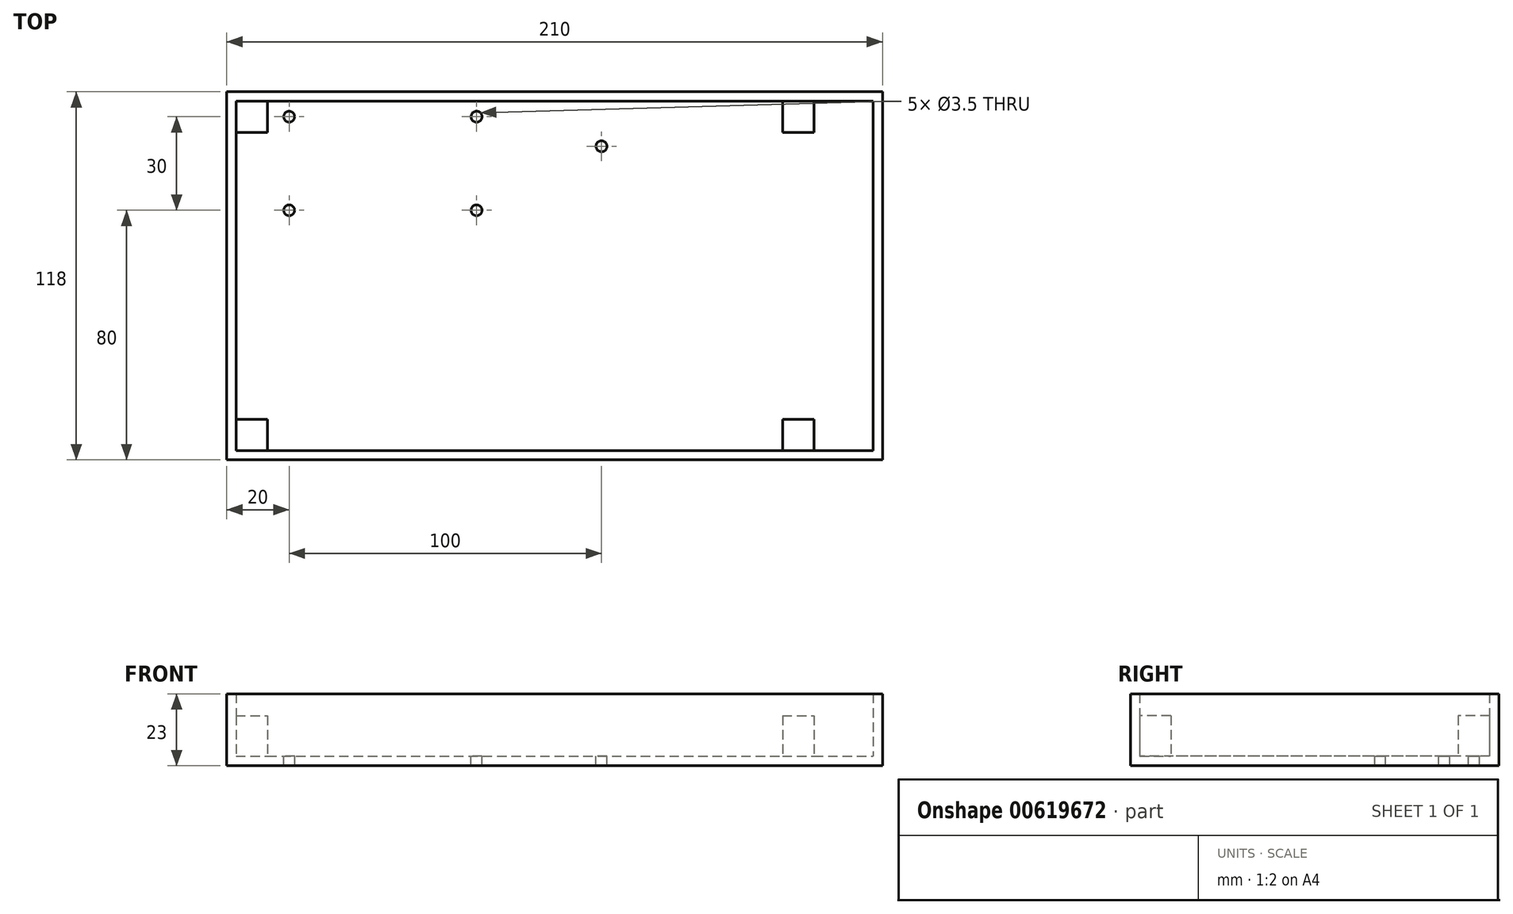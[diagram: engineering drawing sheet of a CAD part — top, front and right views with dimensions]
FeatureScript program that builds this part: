
annotation { "Feature Type Name" : "Feature", "Feature Type Description" : "" }
export const myFeature = defineFeature(function(context is Context, id is Id, definition is map)
    precondition{}
    {
        {
            var Q0;
            Q0=qCreatedBy(makeId("Top.planeOp"),FACE);
            var sketch = newSketch(context, id + "F0", { "sketchPlane" : qUnion([Q0])});
            skLineSegment(sketch, "E0.bottom", {"start": v(0, 0) * mm, "end": v(210, 0) * mm});
            skLineSegment(sketch, "E0.top", {"start": v(0, -118) * mm, "end": v(210, -118) * mm});
            skLineSegment(sketch, "E0.left", {"start": v(0, 0) * mm, "end": v(0, -118) * mm});
            skLineSegment(sketch, "E0.right", {"start": v(210, 0) * mm, "end": v(210, -118) * mm});
            skSolve(sketch);
        }
        {
            var Q0;
            Q0=makeQuery(id+"F0.imprint","IMPRINT",FACE,{"disambiguationData":[TD([[makeQuery(id+"F0.imprint","IMPRINT",EDGE,{"derivedFrom":sQuery(id+"F0.wireOp",EDGE,"E0.bottom")}),-1.0]])]});
            extrude(context, id + "F1", {"entities" : qUnion([Q0]), "depth" : 23 * mm, "offsetDistance" : 25 * mm});
        }
        {
            var Q0;
            Q0=makeQuery(id+"F1.opExtrude","CAP_FACE",FACE,{"disambiguationData":[OSD([sQuery(id+"F0.wireOp",EDGE,"E0.bottom"),sQuery(id+"F0.wireOp",EDGE,"E0.top"),sQuery(id+"F0.wireOp",EDGE,"E0.left"),sQuery(id+"F0.wireOp",EDGE,"E0.right")])],"isStart":false});
            shell(context, id + "F2", {"entities" : qUnion([Q0]), "thickness" : 3 * mm});
        }
        {
            var Q0;
            Q0=makeQuery(id+"F2.opShell","OFFSET_FACE",FACE,{"disambiguationData":[OSD([sQuery(id+"F0.wireOp",EDGE,"E0.bottom"),sQuery(id+"F0.wireOp",EDGE,"E0.top"),sQuery(id+"F0.wireOp",EDGE,"E0.left"),sQuery(id+"F0.wireOp",EDGE,"E0.right")])]});
            var sketch = newSketch(context, id + "F3", { "sketchPlane" : qUnion([Q0])});
            skLineSegment(sketch, "E1", {"start": v(3, -8) * mm, "end": v(207, -8) * mm, "construction": true});
            skLineSegment(sketch, "E2", {"start": v(3, -110) * mm, "end": v(207, -110) * mm, "construction": true});
            skLineSegment(sketch, "E3.bottom", {"start": v(3, -3) * mm, "end": v(13, -3) * mm});
            skLineSegment(sketch, "E3.top", {"start": v(3, -13) * mm, "end": v(13, -13) * mm});
            skLineSegment(sketch, "E3.left", {"start": v(3, -3) * mm, "end": v(3, -13) * mm});
            skLineSegment(sketch, "E3.right", {"start": v(13, -3) * mm, "end": v(13, -13) * mm});
            skLineSegment(sketch, "E4.bottom", {"start": v(178, -3) * mm, "end": v(188, -3) * mm});
            skLineSegment(sketch, "E4.top", {"start": v(178, -13) * mm, "end": v(188, -13) * mm});
            skLineSegment(sketch, "E4.left", {"start": v(178, -3) * mm, "end": v(178, -13) * mm});
            skLineSegment(sketch, "E4.right", {"start": v(188, -3) * mm, "end": v(188, -13) * mm});
            skLineSegment(sketch, "E5.bottom", {"start": v(3, -115) * mm, "end": v(13, -115) * mm});
            skLineSegment(sketch, "E5.top", {"start": v(3, -105) * mm, "end": v(13, -105) * mm});
            skLineSegment(sketch, "E5.left", {"start": v(3, -115) * mm, "end": v(3, -105) * mm});
            skLineSegment(sketch, "E5.right", {"start": v(13, -115) * mm, "end": v(13, -105) * mm});
            skLineSegment(sketch, "E6.bottom", {"start": v(178, -115) * mm, "end": v(188, -115) * mm});
            skLineSegment(sketch, "E6.top", {"start": v(178, -105) * mm, "end": v(188, -105) * mm});
            skLineSegment(sketch, "E6.left", {"start": v(178, -115) * mm, "end": v(178, -105) * mm});
            skLineSegment(sketch, "E6.right", {"start": v(188, -115) * mm, "end": v(188, -105) * mm});
            skSolve(sketch);
        }
        {
            var Q0;
            Q0=makeQuery(id+"F3.imprint","IMPRINT",FACE,{"disambiguationData":[TD([[makeQuery(id+"F3.imprint","IMPRINT",EDGE,{"derivedFrom":sQuery(id+"F3.wireOp",EDGE,"E3.bottom")}),-1.0]])]});
            var Q1;
            Q1=makeQuery(id+"F3.imprint","IMPRINT",FACE,{"disambiguationData":[TD([[makeQuery(id+"F3.imprint","IMPRINT",EDGE,{"derivedFrom":sQuery(id+"F3.wireOp",EDGE,"E4.bottom")}),-1.0]])]});
            var Q2;
            Q2=makeQuery(id+"F3.imprint","IMPRINT",FACE,{"disambiguationData":[TD([[makeQuery(id+"F3.imprint","IMPRINT",EDGE,{"derivedFrom":sQuery(id+"F3.wireOp",EDGE,"E6.bottom")}),1.0]])]});
            var Q3;
            Q3=makeQuery(id+"F3.imprint","IMPRINT",FACE,{"disambiguationData":[TD([[makeQuery(id+"F3.imprint","IMPRINT",EDGE,{"derivedFrom":sQuery(id+"F3.wireOp",EDGE,"E5.bottom")}),1.0]])]});
            extrude(context, id + "F4", {"entities" : qUnion([Q0, Q1, Q2, Q3]), "operationType" : NewBodyOperationType.ADD, "depth" : 13 * mm, "offsetDistance" : 25 * mm});
        }
        {
            var Q0;
            Q0=makeQuery(id+"F2.opShell","OFFSET_FACE",FACE,{"disambiguationData":[OSD([sQuery(id+"F0.wireOp",EDGE,"E0.bottom"),sQuery(id+"F0.wireOp",EDGE,"E0.top"),sQuery(id+"F0.wireOp",EDGE,"E0.left"),sQuery(id+"F0.wireOp",EDGE,"E0.right")])]});
            var sketch = newSketch(context, id + "F5", { "sketchPlane" : qUnion([Q0])});
            skLineSegment(sketch, "E7", {"start": v(3, -8) * mm, "end": v(207, -8) * mm, "construction": true});
            skLineSegment(sketch, "E8", {"start": v(207, -38) * mm, "end": v(3, -38) * mm, "construction": true});
            skCircle(sketch, "E9", {"center": v(20, -8) * mm, "radius": 1.75 * mm});
            skCircle(sketch, "E10", {"center": v(80, -8) * mm, "radius": 1.75 * mm});
            skCircle(sketch, "E11", {"center": v(20, -38) * mm, "radius": 1.75 * mm});
            skCircle(sketch, "E12", {"center": v(80, -38) * mm, "radius": 1.75 * mm});
            skLineSegment(sketch, "E13", {"start": v(207, -17.5) * mm, "end": v(3, -17.5) * mm, "construction": true});
            skCircle(sketch, "E14", {"center": v(120, -17.5) * mm, "radius": 1.75 * mm});
            skSolve(sketch);
        }
        {
            var Q0;
            Q0=makeQuery(id+"F5.imprint","IMPRINT",FACE,{"disambiguationData":[TD([[makeQuery(id+"F5.imprint","IMPRINT",EDGE,{"derivedFrom":sQuery(id+"F5.wireOp",EDGE,"E9")}),1.0]])]});
            var Q1;
            Q1=makeQuery(id+"F5.imprint","IMPRINT",FACE,{"disambiguationData":[TD([[makeQuery(id+"F5.imprint","IMPRINT",EDGE,{"derivedFrom":sQuery(id+"F5.wireOp",EDGE,"E11")}),1.0]])]});
            var Q2;
            Q2=makeQuery(id+"F5.imprint","IMPRINT",FACE,{"disambiguationData":[TD([[makeQuery(id+"F5.imprint","IMPRINT",EDGE,{"derivedFrom":sQuery(id+"F5.wireOp",EDGE,"E12")}),1.0]])]});
            var Q3;
            Q3=makeQuery(id+"F5.imprint","IMPRINT",FACE,{"disambiguationData":[TD([[makeQuery(id+"F5.imprint","IMPRINT",EDGE,{"derivedFrom":sQuery(id+"F5.wireOp",EDGE,"E10")}),1.0]])]});
            var Q4;
            Q4=makeQuery(id+"F5.imprint","IMPRINT",FACE,{"disambiguationData":[TD([[makeQuery(id+"F5.imprint","IMPRINT",EDGE,{"derivedFrom":sQuery(id+"F5.wireOp",EDGE,"E14")}),1.0]])]});
            extrude(context, id + "F6", {"entities" : qUnion([Q0, Q1, Q2, Q3, Q4]), "operationType" : NewBodyOperationType.REMOVE, "oppositeDirection" : true, "depth" : 25 * mm, "offsetDistance" : 25 * mm});
        }
    });
